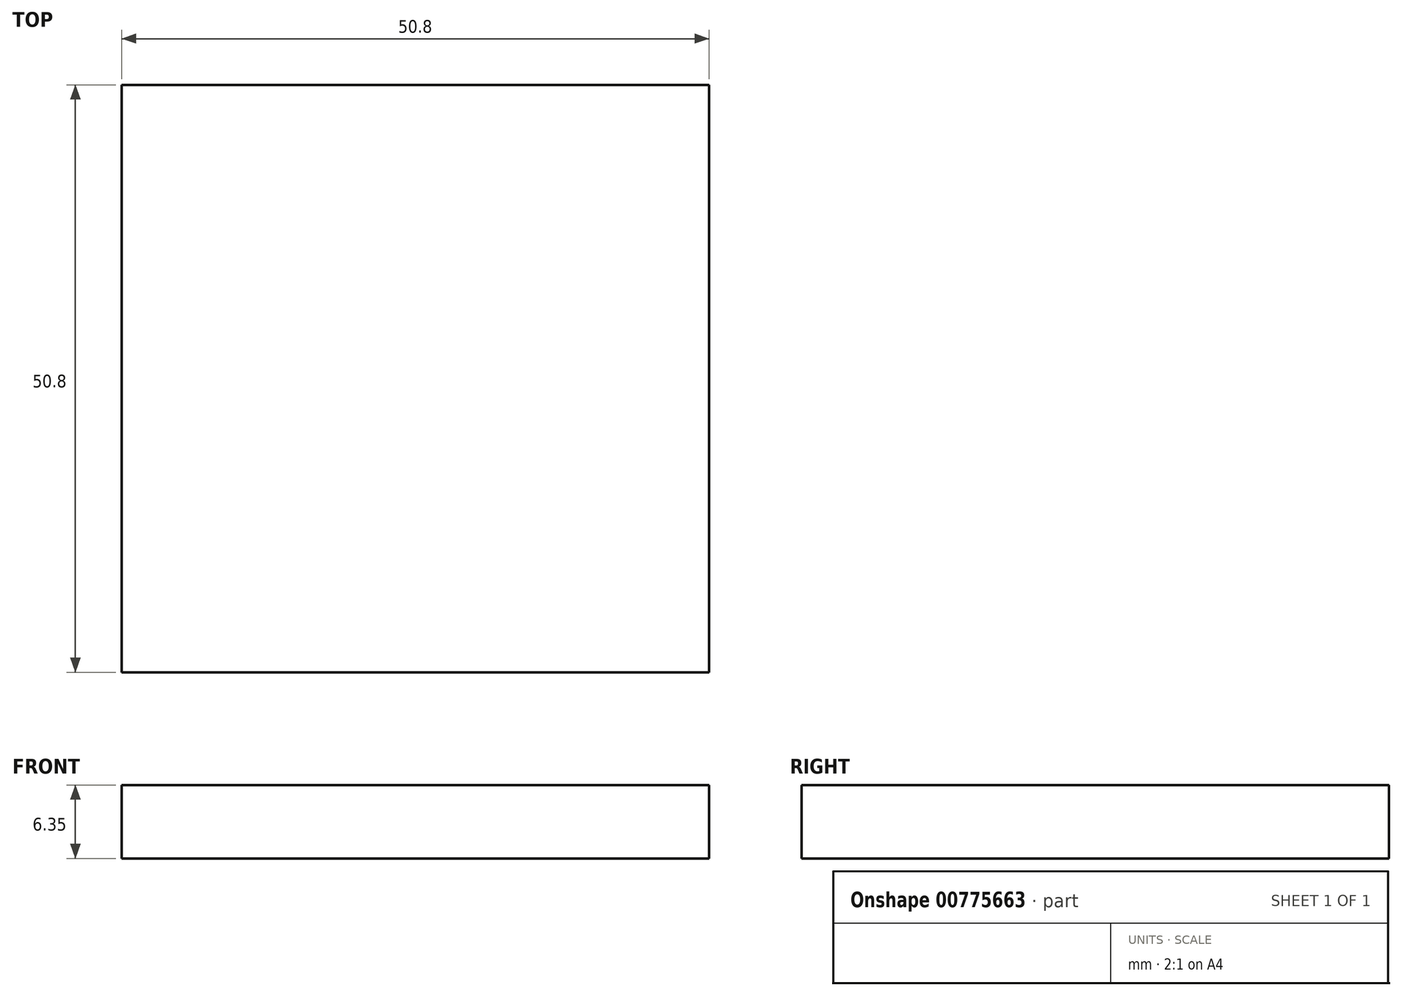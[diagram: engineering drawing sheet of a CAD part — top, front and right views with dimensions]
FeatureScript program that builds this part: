
annotation { "Feature Type Name" : "Feature", "Feature Type Description" : "" }
export const myFeature = defineFeature(function(context is Context, id is Id, definition is map)
    precondition{}
    {
        {
            var Q0;
            Q0=qCreatedBy(makeId("Top.planeOp"),FACE);
            var sketch = newSketch(context, id + "F0", { "sketchPlane" : qUnion([Q0])});
            skLineSegment(sketch, "E0.bottom", {"start": v(25.4, -25.4) * mm, "end": v(-25.4, -25.4) * mm});
            skLineSegment(sketch, "E0.top", {"start": v(25.4, 25.4) * mm, "end": v(-25.4, 25.4) * mm});
            skLineSegment(sketch, "E0.left", {"start": v(25.4, -25.4) * mm, "end": v(25.4, 25.4) * mm});
            skLineSegment(sketch, "E0.right", {"start": v(-25.4, -25.4) * mm, "end": v(-25.4, 25.4) * mm});
            skPoint(sketch, "E0.middle", {"position": v(0, 0) * mm});
            skSolve(sketch);
        }
        {
            var Q0;
            Q0=makeQuery(id+"F0.imprint","IMPRINT",FACE,{"disambiguationData":[TD([[makeQuery(id+"F0.imprint","IMPRINT",EDGE,{"derivedFrom":sQuery(id+"F0.wireOp",EDGE,"E0.bottom")}),-1.0]])]});
            extrude(context, id + "F1", {"entities" : qUnion([Q0]), "depth" : 6.35 * mm, "offsetDistance" : 25 * mm});
        }
    });
